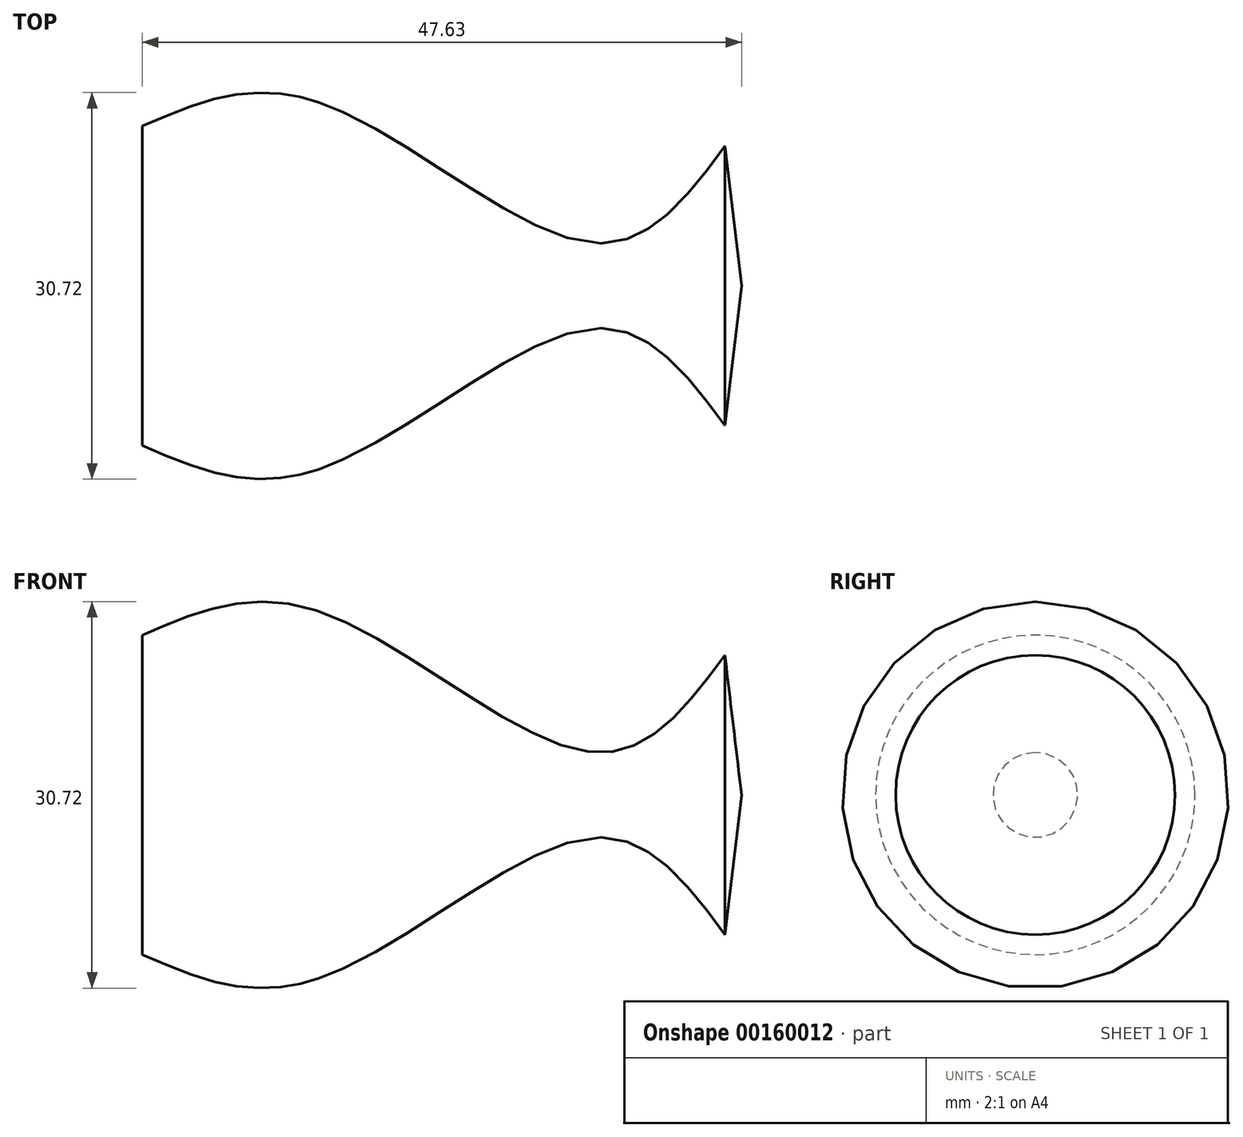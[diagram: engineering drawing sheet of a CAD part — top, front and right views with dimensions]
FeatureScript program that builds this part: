
annotation { "Feature Type Name" : "Feature", "Feature Type Description" : "" }
export const myFeature = defineFeature(function(context is Context, id is Id, definition is map)
    precondition{}
    {
        {
            var Q0;
            Q0=qCreatedBy(makeId("Front.planeOp"),FACE);
            var sketch = newSketch(context, id + "F0", { "sketchPlane" : qUnion([Q0])});
            skLineSegment(sketch, "E0", {"start": v(0, 0) * mm, "end": v(0, 12.7) * mm});
            skFitSpline(sketch, "E1", {"points": [v(0, 12.7) * mm, v(13.74, 14.68) * mm, v(35.96, 3.39) * mm, v(46.31, 11.1) * mm], "startDerivative": vector(41.91, 18.26) * mm, "endDerivative": vector(30.45, 41.1) * mm});
            skLineSegment(sketch, "E2", {"start": v(46.31, 11.1) * mm, "end": v(47.63, 0) * mm});
            skLineSegment(sketch, "E3", {"start": v(47.63, 0) * mm, "end": v(0, 0) * mm});
            skLineSegment(sketch, "E4", {"start": v(0, 0) * mm, "end": v(-76.8, 0) * mm});
            skLineSegment(sketch, "E5", {"start": v(-76.8, 0) * mm, "end": v(74.55, 0) * mm});
            skSolve(sketch);
        }
        {
            var Q0;
            {var subQ0=sQuery(id+"F0.wireOp",EDGE,"E0");Q0=makeQuery(id+"F0.imprint","IMPRINT",FACE,{"disambiguationData":[TD([[makeQuery(id+"F0.imprint","IMPRINT",EDGE,{"derivedFrom":subQ0}),-1.0]])]});}
            var Q1;
            Q1=sQuery(id+"F0.wireOp",EDGE,"E5");
            revolve(context, id + "F1", {"entities" : qUnion([Q0]), "axis" : qUnion([Q1]), "revolveType" : RevolveType.FULL});
        }
    });
